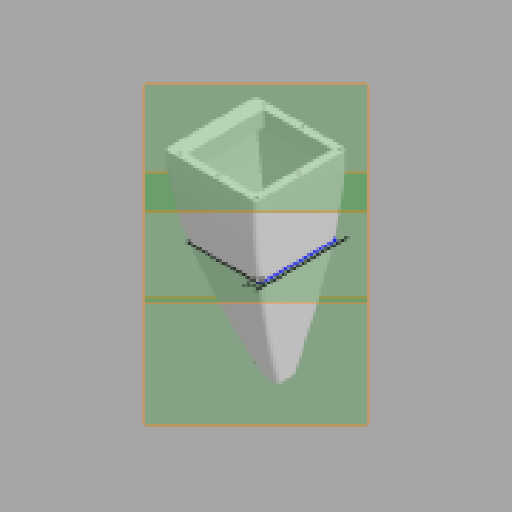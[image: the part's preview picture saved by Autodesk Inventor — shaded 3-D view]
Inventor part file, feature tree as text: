
AUTODESK INVENTOR PART (.ipt)
format: ipt  version: 2025 (Build 290162000, 162)  size: 603,648 bytes
history: native  units: in
note: dims shown in document units (in); Inventor stores cm internally (conversion verified against a paired STEP export)
features: sketch x10, extrude x5, fillet x4, plane x3, loft x1, shell x1, other x1
ambient origin geometry x8: Origin, YZ Plane, XZ Plane, XY Plane, X Axis, Y Axis, Z Axis, Center Point
bodies: Solid1 (feature_tree)
feature tree (25):
  sketch  "Sketch1"  dims[d0=6.0in d1=6.0in]
  plane  "Work Plane1"
  plane  "Work Plane2"
  sketch  "Sketch2"  dims[d2=5.5in d7=12.0in d10=1.0in d11=0.0in d12=5.0in]
  extrude  "Extrusion1"  Depth=6.0in
  sketch  "3D Sketch1"
  plane  "Work Plane3"
  sketch  "Sketch3"  dims[d24=0.6in d25=0.6in]
  loft  "Loft1"
  sketch  "Sketch4"  dims[d26=0.0in d27=90.0deg d28=0.0in d29=90.0deg d30=0.0in d31=90.0deg d32=0.0in d33=90.0deg d38=0.25in d39=0.0in d40=90.0deg]
  fillet  "Fillet1"  Radius=1.0in
  fillet  "Fillet2"  Radius=5.0in
  extrude  "Extrusion3"  Depth=0.6in
  extrude  "Extrusion4"  Depth=0.25in
  shell  "Shell2"  Thickness=0.0in
  extrude  "Extrusion5"  Depth=0.25in
  extrude  "Extrusion6"  Depth=0.5in TaperAngle=0.0deg
  fillet  "Fillet3"  Radius=0.25in
  fillet  "Fillet4"  Radius=2.5in
  sketch  "3D Sketch7"
  other  "Edges1"
  sketch  "Sketch5"  dims[d41=0.0in d42=90.0deg d44=0.25in]
  sketch  "Sketch7"  dims[d45=0.25in d51=0.5in d52=0.0in d54=0.25in d55=2.5in]
  sketch  "Sketch8"  dims[d56=2.5in]
  sketch  "Sketch9"  dims[d57=0.25in d58=0.5in d59=0.0in d60=0.15in d61=2.5in d62=2.5in d64=0.712in d65=0.712in d66=0.726in d67=0.1in d68=0.0in d69=0.16in d70=12.0in d71=0.0in d72=0.3in d73=0.25in d53=0.5in d74=0.0in d75=0.0in d76=0.0in d77=0.0in]
